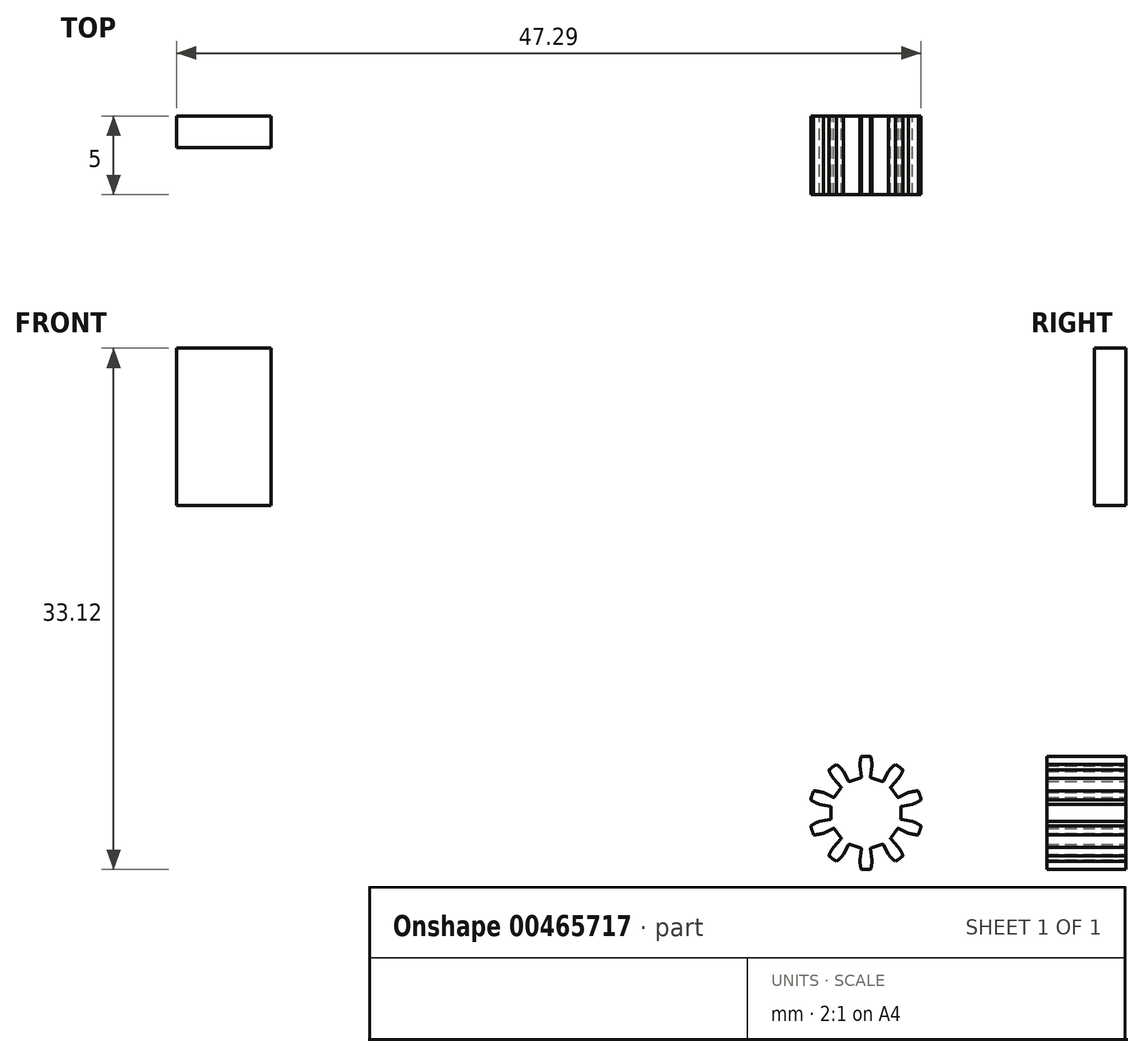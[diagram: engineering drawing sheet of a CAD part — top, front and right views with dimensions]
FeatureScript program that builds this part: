
annotation { "Feature Type Name" : "Feature", "Feature Type Description" : "" }
export const myFeature = defineFeature(function(context is Context, id is Id, definition is map)
    precondition{}
    {
        {
            var Q0;
            Q0=qCreatedBy(makeId("Front.planeOp"),FACE);
            var sketch = newSketch(context, id + "F0", { "sketchPlane" : qUnion([Q0])});
            skCircle(sketch, "E0", {"center": v(0, 0) * mm, "radius": 1.5 * mm, "construction": true});
            skCircle(sketch, "E1", {"center": v(0, 0) * mm, "radius": 3 * mm, "construction": true});
            skCircle(sketch, "E2", {"center": v(0, 0) * mm, "radius": 3.6 * mm, "construction": true});
            skCircle(sketch, "E3", {"center": v(0, 0) * mm, "radius": 2.25 * mm, "construction": true});
            skLineSegment(sketch, "E4", {"start": v(0, 0) * mm, "end": v(0, 4.8) * mm, "construction": true});
            skLineSegment(sketch, "E5", {"start": v(0, 0) * mm, "end": v(-2.88, 3.97) * mm, "construction": true});
            skLineSegment(sketch, "E6", {"start": v(0, 0) * mm, "end": v(2.78, 3.82) * mm, "construction": true});
            skArc(sketch, "E7", {"start": v(0.3, 3.59) * mm, "mid": v(0, 3.6) * mm, "end": v(-0.3, 3.59) * mm});
            skArc(sketch, "E8", {"start": v(-0.3, 3.59) * mm, "mid": v(-0.36, 3.28) * mm, "end": v(-0.4, 2.97) * mm});
            skArc(sketch, "E9", {"start": v(-1.43, 2.64) * mm, "mid": v(-1.63, 2.87) * mm, "end": v(-1.87, 3.08) * mm});
            skArc(sketch, "E10", {"start": v(-1.87, 3.08) * mm, "mid": v(-2.12, 2.91) * mm, "end": v(-2.35, 2.73) * mm});
            skLineSegment(sketch, "E11", {"start": v(0, 0) * mm, "end": v(-5.07, 1.65) * mm, "construction": true});
            skArc(sketch, "E12.MirrorCS", {"start": v(0.3, 3.59) * mm, "mid": v(0.36, 3.28) * mm, "end": v(0.4, 2.97) * mm});
            skArc(sketch, "E13.MirrorCS", {"start": v(1.43, 2.64) * mm, "mid": v(1.63, 2.87) * mm, "end": v(1.87, 3.08) * mm});
            skArc(sketch, "E14.MirrorCS", {"start": v(1.87, 3.08) * mm, "mid": v(2.12, 2.91) * mm, "end": v(2.35, 2.73) * mm});
            skArc(sketch, "E15.MirrorCS", {"start": v(-0.3, 3.59) * mm, "mid": v(0, 3.6) * mm, "end": v(0.3, 3.59) * mm});
            skArc(sketch, "E16.MirrorCS", {"start": v(2.35, 2.73) * mm, "mid": v(2.12, 2.91) * mm, "end": v(1.87, 3.08) * mm});
            skArc(sketch, "E17.MirrorCS", {"start": v(3.5, -0.82) * mm, "mid": v(3.42, -1.11) * mm, "end": v(3.32, -1.4) * mm});
            skArc(sketch, "E18.MirrorCS", {"start": v(3.5, 0.82) * mm, "mid": v(3.24, 0.67) * mm, "end": v(2.95, 0.55) * mm});
            skArc(sketch, "E19.MirrorCS", {"start": v(2.07, 2.18) * mm, "mid": v(2.23, 2.44) * mm, "end": v(2.35, 2.73) * mm});
            skArc(sketch, "E20.MirrorCS", {"start": v(3.5, 0.82) * mm, "mid": v(3.42, 1.11) * mm, "end": v(3.32, 1.4) * mm, "construction": true});
            skArc(sketch, "E21.MirrorCS", {"start": v(2.95, -0.55) * mm, "mid": v(3.24, -0.67) * mm, "end": v(3.5, -0.82) * mm});
            skArc(sketch, "E22.MirrorCS", {"start": v(3.32, 1.4) * mm, "mid": v(3.01, 1.36) * mm, "end": v(2.7, 1.3) * mm});
            skArc(sketch, "E23.MirrorCS", {"start": v(3.32, 1.4) * mm, "mid": v(3.42, 1.11) * mm, "end": v(3.5, 0.82) * mm});
            skArc(sketch, "E24.MirrorCS", {"start": v(3.5, -0.82) * mm, "mid": v(3.24, -0.67) * mm, "end": v(2.95, -0.55) * mm});
            skArc(sketch, "E25.MirrorCS", {"start": v(2.07, -2.18) * mm, "mid": v(2.23, -2.44) * mm, "end": v(2.35, -2.73) * mm});
            skArc(sketch, "E26.MirrorCS", {"start": v(3.32, -1.4) * mm, "mid": v(3.01, -1.36) * mm, "end": v(2.7, -1.3) * mm});
            skArc(sketch, "E27.MirrorCS", {"start": v(1.43, -2.64) * mm, "mid": v(1.63, -2.87) * mm, "end": v(1.87, -3.08) * mm});
            skArc(sketch, "E28.MirrorCS", {"start": v(0.3, -3.59) * mm, "mid": v(0.36, -3.28) * mm, "end": v(0.4, -2.97) * mm});
            skArc(sketch, "E29.MirrorCS", {"start": v(3.32, -1.4) * mm, "mid": v(3.42, -1.11) * mm, "end": v(3.5, -0.82) * mm, "construction": true});
            skArc(sketch, "E30.MirrorCS", {"start": v(2.35, -2.73) * mm, "mid": v(2.12, -2.91) * mm, "end": v(1.87, -3.08) * mm});
            skArc(sketch, "E31.MirrorCS", {"start": v(1.87, -3.08) * mm, "mid": v(2.12, -2.91) * mm, "end": v(2.35, -2.73) * mm});
            skArc(sketch, "E32.MirrorCS", {"start": v(-3.5, -0.82) * mm, "mid": v(-3.24, -0.67) * mm, "end": v(-2.95, -0.55) * mm});
            skArc(sketch, "E33.MirrorCS", {"start": v(-3.5, -0.82) * mm, "mid": v(-3.42, -1.11) * mm, "end": v(-3.32, -1.4) * mm});
            skArc(sketch, "E34.MirrorCS", {"start": v(-2.95, -0.55) * mm, "mid": v(-3.24, -0.67) * mm, "end": v(-3.5, -0.82) * mm});
            skArc(sketch, "E35.MirrorCS", {"start": v(-3.5, -0.82) * mm, "mid": v(-3.42, -1.11) * mm, "end": v(-3.32, -1.4) * mm, "construction": true});
            skArc(sketch, "E36.MirrorCS", {"start": v(-3.32, -1.4) * mm, "mid": v(-3.42, -1.11) * mm, "end": v(-3.5, -0.82) * mm, "construction": true});
            skArc(sketch, "E37.MirrorCS", {"start": v(-3.5, 0.82) * mm, "mid": v(-3.42, 1.11) * mm, "end": v(-3.32, 1.4) * mm, "construction": true});
            skArc(sketch, "E38.MirrorCS", {"start": v(-3.32, -1.4) * mm, "mid": v(-3.01, -1.36) * mm, "end": v(-2.7, -1.3) * mm});
            skArc(sketch, "E39.MirrorCS", {"start": v(-2.07, -2.18) * mm, "mid": v(-2.23, -2.44) * mm, "end": v(-2.35, -2.73) * mm});
            skArc(sketch, "E40.MirrorCS", {"start": v(-3.32, 1.4) * mm, "mid": v(-3.01, 1.36) * mm, "end": v(-2.7, 1.3) * mm});
            skArc(sketch, "E41.MirrorCS", {"start": v(-1.87, -3.08) * mm, "mid": v(-2.12, -2.91) * mm, "end": v(-2.35, -2.73) * mm});
            skArc(sketch, "E42.MirrorCS", {"start": v(-1.43, -2.64) * mm, "mid": v(-1.63, -2.87) * mm, "end": v(-1.87, -3.08) * mm});
            skArc(sketch, "E43.MirrorCS", {"start": v(-3.5, 0.82) * mm, "mid": v(-3.24, 0.67) * mm, "end": v(-2.95, 0.55) * mm});
            skArc(sketch, "E44.MirrorCS", {"start": v(-2.07, 2.18) * mm, "mid": v(-2.23, 2.44) * mm, "end": v(-2.35, 2.73) * mm});
            skArc(sketch, "E45.MirrorCS", {"start": v(-0.3, 3.59) * mm, "mid": v(0, 3.6) * mm, "end": v(0.3, 3.59) * mm, "construction": true});
            skArc(sketch, "E46.MirrorCS", {"start": v(-2.35, -2.73) * mm, "mid": v(-2.12, -2.91) * mm, "end": v(-1.87, -3.08) * mm});
            skArc(sketch, "E47.MirrorCS", {"start": v(-3.32, 1.4) * mm, "mid": v(-3.42, 1.11) * mm, "end": v(-3.5, 0.82) * mm});
            skArc(sketch, "E48.MirrorCS", {"start": v(0.3, 3.59) * mm, "mid": v(0, 3.6) * mm, "end": v(-0.3, 3.59) * mm, "construction": true});
            skArc(sketch, "E49.MirrorCS", {"start": v(-2.35, 2.73) * mm, "mid": v(-2.12, 2.91) * mm, "end": v(-1.87, 3.08) * mm});
            skArc(sketch, "E50.MirrorCS", {"start": v(-0.3, -3.59) * mm, "mid": v(-0.36, -3.28) * mm, "end": v(-0.4, -2.97) * mm});
            skLineSegment(sketch, "E51.MirrorCS", {"start": v(0, 0) * mm, "end": v(-2.78, 3.82) * mm, "construction": true});
            skArc(sketch, "E52.MirrorCS", {"start": v(0.3, -3.59) * mm, "mid": v(0, -3.6) * mm, "end": v(-0.3, -3.59) * mm});
            skArc(sketch, "E53.MirrorCS", {"start": v(-0.3, -3.59) * mm, "mid": v(0, -3.6) * mm, "end": v(0.3, -3.59) * mm, "construction": true});
            skArc(sketch, "E54.MirrorCS", {"start": v(0.3, -3.59) * mm, "mid": v(0, -3.6) * mm, "end": v(-0.3, -3.59) * mm, "construction": true});
            skLineSegment(sketch, "E55", {"start": v(-1.43, 2.64) * mm, "end": v(-1.1, 2.02) * mm});
            skLineSegment(sketch, "E56", {"start": v(-1.03, 2) * mm, "end": v(-0.34, 2.22) * mm});
            skLineSegment(sketch, "E57", {"start": v(-0.3, 2.28) * mm, "end": v(-0.4, 2.97) * mm});
            skPoint(sketch, "E58.visualSharp", {"position": v(-1.07, 1.98) * mm});
            skArc(sketch, "E58.filletArc", {"start": v(-1.1, 2.02) * mm, "mid": v(-1.07, 2) * mm, "end": v(-1.03, 2) * mm});
            skPoint(sketch, "E59.visualSharp", {"position": v(-0.3, 2.23) * mm});
            skArc(sketch, "E59.filletArc", {"start": v(-0.34, 2.22) * mm, "mid": v(-0.3, 2.24) * mm, "end": v(-0.3, 2.28) * mm});
            skLineSegment(sketch, "E60", {"start": v(0, 0) * mm, "end": v(-1.43, 2.64) * mm, "construction": true});
            skLineSegment(sketch, "E61", {"start": v(0, 0) * mm, "end": v(-0.4, 2.97) * mm, "construction": true});
            skArc(sketch, "E62.MirrorCS", {"start": v(1.1, 2.02) * mm, "mid": v(1.07, 2) * mm, "end": v(1.03, 2) * mm});
            skArc(sketch, "E63.MirrorCS", {"start": v(0.34, 2.22) * mm, "mid": v(0.3, 2.24) * mm, "end": v(0.3, 2.28) * mm});
            skLineSegment(sketch, "E64.MirrorCS", {"start": v(0.3, 2.28) * mm, "end": v(0.4, 2.97) * mm});
            skPoint(sketch, "E65.MirrorP", {"position": v(1.07, 1.98) * mm});
            skLineSegment(sketch, "E66.MirrorCS", {"start": v(1.03, 2) * mm, "end": v(0.34, 2.22) * mm});
            skLineSegment(sketch, "E67.MirrorCS", {"start": v(1.43, 2.64) * mm, "end": v(1.1, 2.02) * mm});
            skPoint(sketch, "E68.MirrorP", {"position": v(0.3, 2.23) * mm});
            skArc(sketch, "E69.MirrorCS", {"start": v(-0.34, -2.22) * mm, "mid": v(-0.3, -2.24) * mm, "end": v(-0.3, -2.28) * mm});
            skArc(sketch, "E70.MirrorCS", {"start": v(-1.1, -2.02) * mm, "mid": v(-1.07, -2) * mm, "end": v(-1.03, -2) * mm});
            skArc(sketch, "E71.MirrorCS", {"start": v(-0.3, -3.59) * mm, "mid": v(0, -3.6) * mm, "end": v(0.3, -3.59) * mm});
            skArc(sketch, "E72.MirrorCS", {"start": v(0.34, -2.22) * mm, "mid": v(0.3, -2.24) * mm, "end": v(0.3, -2.28) * mm});
            skArc(sketch, "E73.MirrorCS", {"start": v(1.1, -2.02) * mm, "mid": v(1.07, -2) * mm, "end": v(1.03, -2) * mm});
            skPoint(sketch, "E74.MirrorP", {"position": v(-0.3, -2.23) * mm});
            skLineSegment(sketch, "E75.MirrorCS", {"start": v(-0.3, -2.28) * mm, "end": v(-0.4, -2.97) * mm});
            skPoint(sketch, "E76.MirrorP", {"position": v(0.3, -2.23) * mm});
            skLineSegment(sketch, "E77.MirrorCS", {"start": v(1.43, -2.64) * mm, "end": v(1.1, -2.02) * mm});
            skLineSegment(sketch, "E78.MirrorCS", {"start": v(-1.03, -2) * mm, "end": v(-0.34, -2.22) * mm});
            skPoint(sketch, "E79.MirrorP", {"position": v(1.07, -1.98) * mm});
            skPoint(sketch, "E80.MirrorP", {"position": v(-1.07, -1.98) * mm});
            skLineSegment(sketch, "E81.MirrorCS", {"start": v(-1.43, -2.64) * mm, "end": v(-1.1, -2.02) * mm});
            skLineSegment(sketch, "E82.MirrorCS", {"start": v(1.03, -2) * mm, "end": v(0.34, -2.22) * mm});
            skLineSegment(sketch, "E83.MirrorCS", {"start": v(0.3, -2.28) * mm, "end": v(0.4, -2.97) * mm});
            skArc(sketch, "E84.MirrorCS", {"start": v(3.32, -1.4) * mm, "mid": v(3.42, -1.11) * mm, "end": v(3.5, -0.82) * mm});
            skArc(sketch, "E85.MirrorCS", {"start": v(3.5, 0.82) * mm, "mid": v(3.42, 1.11) * mm, "end": v(3.32, 1.4) * mm});
            skArc(sketch, "E86.MirrorCS", {"start": v(2, 1) * mm, "mid": v(2.03, 0.99) * mm, "end": v(2.07, 0.99) * mm});
            skArc(sketch, "E87.MirrorCS", {"start": v(-3.32, -1.4) * mm, "mid": v(-3.42, -1.11) * mm, "end": v(-3.5, -0.82) * mm});
            skArc(sketch, "E88.MirrorCS", {"start": v(2.21, 0.36) * mm, "mid": v(2.23, 0.4) * mm, "end": v(2.26, 0.42) * mm});
            skArc(sketch, "E89.MirrorCS", {"start": v(3.32, 1.4) * mm, "mid": v(3.42, 1.11) * mm, "end": v(3.5, 0.82) * mm, "construction": true});
            skArc(sketch, "E90.MirrorCS", {"start": v(-2.26, 0.42) * mm, "mid": v(-2.23, 0.4) * mm, "end": v(-2.21, 0.36) * mm});
            skArc(sketch, "E91.MirrorCS", {"start": v(-3.5, 0.82) * mm, "mid": v(-3.42, 1.11) * mm, "end": v(-3.32, 1.4) * mm});
            skArc(sketch, "E92.MirrorCS", {"start": v(-2.21, -0.36) * mm, "mid": v(-2.23, -0.4) * mm, "end": v(-2.26, -0.42) * mm});
            skArc(sketch, "E93.MirrorCS", {"start": v(-2.35, 2.73) * mm, "mid": v(-2.12, 2.91) * mm, "end": v(-1.87, 3.08) * mm, "construction": true});
            skArc(sketch, "E94.MirrorCS", {"start": v(1.87, -3.08) * mm, "mid": v(2.12, -2.91) * mm, "end": v(2.35, -2.73) * mm, "construction": true});
            skArc(sketch, "E95.MirrorCS", {"start": v(-1.58, -1.67) * mm, "mid": v(-1.57, -1.63) * mm, "end": v(-1.58, -1.6) * mm});
            skArc(sketch, "E96.MirrorCS", {"start": v(2.26, -0.42) * mm, "mid": v(2.23, -0.4) * mm, "end": v(2.21, -0.36) * mm});
            skArc(sketch, "E97.MirrorCS", {"start": v(-2, -1) * mm, "mid": v(-2.03, -0.99) * mm, "end": v(-2.07, -0.99) * mm});
            skArc(sketch, "E98.MirrorCS", {"start": v(1.58, 1.67) * mm, "mid": v(1.57, 1.63) * mm, "end": v(1.58, 1.6) * mm});
            skArc(sketch, "E99.MirrorCS", {"start": v(-1.87, 3.08) * mm, "mid": v(-1.63, 2.87) * mm, "end": v(-1.43, 2.64) * mm});
            skArc(sketch, "E100.MirrorCS", {"start": v(0.4, -2.97) * mm, "mid": v(0.36, -3.28) * mm, "end": v(0.3, -3.59) * mm});
            skArc(sketch, "E101.MirrorCS", {"start": v(-2.95, 0.55) * mm, "mid": v(-3.24, 0.67) * mm, "end": v(-3.5, 0.82) * mm});
            skLineSegment(sketch, "E102.MirrorCS", {"start": v(2.21, -0.36) * mm, "end": v(2.21, 0.36) * mm});
            skLineSegment(sketch, "E103.MirrorCS", {"start": v(2.26, 0.42) * mm, "end": v(2.95, 0.55) * mm});
            skArc(sketch, "E104.MirrorCS", {"start": v(-2.7, 1.3) * mm, "mid": v(-3.01, 1.36) * mm, "end": v(-3.32, 1.4) * mm});
            skArc(sketch, "E105.MirrorCS", {"start": v(-2.35, 2.73) * mm, "mid": v(-2.23, 2.44) * mm, "end": v(-2.07, 2.18) * mm});
            skLineSegment(sketch, "E106.MirrorCS", {"start": v(2.95, -0.55) * mm, "end": v(2.26, -0.42) * mm});
            skLineSegment(sketch, "E107.MirrorCS", {"start": v(0, 0) * mm, "end": v(4.66, -1.52) * mm, "construction": true});
            skArc(sketch, "E108.MirrorCS", {"start": v(2.35, -2.73) * mm, "mid": v(2.23, -2.44) * mm, "end": v(2.07, -2.18) * mm});
            skArc(sketch, "E109.MirrorCS", {"start": v(1.87, -3.08) * mm, "mid": v(1.63, -2.87) * mm, "end": v(1.43, -2.64) * mm});
            skLineSegment(sketch, "E110.MirrorCS", {"start": v(0, 0) * mm, "end": v(4.56, 1.48) * mm, "construction": true});
            skArc(sketch, "E111.MirrorCS", {"start": v(2.7, -1.3) * mm, "mid": v(3.01, -1.36) * mm, "end": v(3.32, -1.4) * mm});
            skPoint(sketch, "E112.MirrorP", {"position": v(2.21, -0.4) * mm});
            skLineSegment(sketch, "E113.MirrorCS", {"start": v(0, 0) * mm, "end": v(4.5, -1.46) * mm, "construction": true});
            skLineSegment(sketch, "E114.MirrorCS", {"start": v(-2.95, 0.55) * mm, "end": v(-2.26, 0.42) * mm});
            skLineSegment(sketch, "E115.MirrorCS", {"start": v(-2.07, -0.99) * mm, "end": v(-2.7, -1.3) * mm});
            skPoint(sketch, "E116.MirrorP", {"position": v(-2.21, -0.4) * mm});
            skPoint(sketch, "E117.MirrorP", {"position": v(-2.21, 0.4) * mm});
            skLineSegment(sketch, "E118.MirrorCS", {"start": v(-1.58, -1.6) * mm, "end": v(-2, -1) * mm});
            skLineSegment(sketch, "E119.MirrorCS", {"start": v(-2.26, -0.42) * mm, "end": v(-2.95, -0.55) * mm});
            skLineSegment(sketch, "E120.MirrorCS", {"start": v(0, 0) * mm, "end": v(2.95, 0.55) * mm, "construction": true});
            skLineSegment(sketch, "E121.MirrorCS", {"start": v(2.07, 0.99) * mm, "end": v(2.7, 1.3) * mm});
            skPoint(sketch, "E122.MirrorP", {"position": v(1.55, 1.63) * mm});
            skPoint(sketch, "E123.MirrorP", {"position": v(2.21, 0.4) * mm});
            skLineSegment(sketch, "E124.MirrorCS", {"start": v(1.58, 1.6) * mm, "end": v(2, 1) * mm});
            skLineSegment(sketch, "E125.MirrorCS", {"start": v(2.07, 2.18) * mm, "end": v(1.58, 1.67) * mm});
            skPoint(sketch, "E126.MirrorP", {"position": v(-2.03, -0.97) * mm});
            skLineSegment(sketch, "E127.MirrorCS", {"start": v(0, 0) * mm, "end": v(2.95, -0.55) * mm, "construction": true});
            skPoint(sketch, "E128.MirrorP", {"position": v(2.03, 0.97) * mm});
            skPoint(sketch, "E129.MirrorP", {"position": v(-1.55, -1.63) * mm});
            skLineSegment(sketch, "E130.MirrorCS", {"start": v(-2.07, -2.18) * mm, "end": v(-1.58, -1.67) * mm});
            skLineSegment(sketch, "E131.MirrorCS", {"start": v(-2.21, 0.36) * mm, "end": v(-2.21, -0.36) * mm});
            skArc(sketch, "E132.MirrorCS", {"start": v(3.5, -0.82) * mm, "mid": v(3.42, -1.11) * mm, "end": v(3.32, -1.4) * mm, "construction": true});
            skArc(sketch, "E133.MirrorCS", {"start": v(2.35, 2.73) * mm, "mid": v(2.12, 2.91) * mm, "end": v(1.87, 3.08) * mm, "construction": true});
            skArc(sketch, "E134.MirrorCS", {"start": v(-3.32, 1.4) * mm, "mid": v(-3.42, 1.11) * mm, "end": v(-3.5, 0.82) * mm, "construction": true});
            skArc(sketch, "E135.MirrorCS", {"start": v(-1.87, -3.08) * mm, "mid": v(-2.12, -2.91) * mm, "end": v(-2.35, -2.73) * mm, "construction": true});
            skArc(sketch, "E136.MirrorCS", {"start": v(-0.4, -2.97) * mm, "mid": v(-0.36, -3.28) * mm, "end": v(-0.3, -3.59) * mm});
            skArc(sketch, "E137.MirrorCS", {"start": v(1.87, 3.08) * mm, "mid": v(1.63, 2.87) * mm, "end": v(1.43, 2.64) * mm});
            skArc(sketch, "E138.MirrorCS", {"start": v(2, -1) * mm, "mid": v(2.03, -0.99) * mm, "end": v(2.07, -0.99) * mm});
            skArc(sketch, "E139.MirrorCS", {"start": v(-1.58, 1.67) * mm, "mid": v(-1.57, 1.63) * mm, "end": v(-1.58, 1.6) * mm});
            skArc(sketch, "E140.MirrorCS", {"start": v(2.26, 0.42) * mm, "mid": v(2.23, 0.4) * mm, "end": v(2.21, 0.36) * mm});
            skArc(sketch, "E141.MirrorCS", {"start": v(-2, 1) * mm, "mid": v(-2.03, 0.99) * mm, "end": v(-2.07, 0.99) * mm});
            skArc(sketch, "E142.MirrorCS", {"start": v(-2.21, 0.36) * mm, "mid": v(-2.23, 0.4) * mm, "end": v(-2.26, 0.42) * mm});
            skArc(sketch, "E143.MirrorCS", {"start": v(-2.26, -0.42) * mm, "mid": v(-2.23, -0.4) * mm, "end": v(-2.21, -0.36) * mm});
            skArc(sketch, "E144.MirrorCS", {"start": v(1.58, -1.67) * mm, "mid": v(1.57, -1.63) * mm, "end": v(1.58, -1.6) * mm});
            skArc(sketch, "E145.MirrorCS", {"start": v(-2.7, -1.3) * mm, "mid": v(-3.01, -1.36) * mm, "end": v(-3.32, -1.4) * mm});
            skArc(sketch, "E146.MirrorCS", {"start": v(-2.35, -2.73) * mm, "mid": v(-2.23, -2.44) * mm, "end": v(-2.07, -2.18) * mm});
            skArc(sketch, "E147.MirrorCS", {"start": v(2.21, -0.36) * mm, "mid": v(2.23, -0.4) * mm, "end": v(2.26, -0.42) * mm});
            skArc(sketch, "E148.MirrorCS", {"start": v(-1.87, -3.08) * mm, "mid": v(-1.63, -2.87) * mm, "end": v(-1.43, -2.64) * mm});
            skLineSegment(sketch, "E149.MirrorCS", {"start": v(0, 0) * mm, "end": v(2.88, 3.97) * mm, "construction": true});
            skLineSegment(sketch, "E150.MirrorCS", {"start": v(-2.95, -0.55) * mm, "end": v(-2.26, -0.42) * mm});
            skLineSegment(sketch, "E151.MirrorCS", {"start": v(0, 0) * mm, "end": v(-4.5, -1.46) * mm, "construction": true});
            skArc(sketch, "E152.MirrorCS", {"start": v(2.35, 2.73) * mm, "mid": v(2.23, 2.44) * mm, "end": v(2.07, 2.18) * mm});
            skLineSegment(sketch, "E153.MirrorCS", {"start": v(-2.26, 0.42) * mm, "end": v(-2.95, 0.55) * mm});
            skArc(sketch, "E154.MirrorCS", {"start": v(2.7, 1.3) * mm, "mid": v(3.01, 1.36) * mm, "end": v(3.32, 1.4) * mm});
            skLineSegment(sketch, "E155.MirrorCS", {"start": v(0, 0) * mm, "end": v(-4.56, 1.48) * mm, "construction": true});
            skArc(sketch, "E156.MirrorCS", {"start": v(2.95, 0.55) * mm, "mid": v(3.24, 0.67) * mm, "end": v(3.5, 0.82) * mm});
            skLineSegment(sketch, "E157.MirrorCS", {"start": v(0, 0) * mm, "end": v(-4.66, -1.52) * mm, "construction": true});
            skPoint(sketch, "E158.MirrorP", {"position": v(-2.03, 0.97) * mm});
            skLineSegment(sketch, "E159.MirrorCS", {"start": v(2.07, -0.99) * mm, "end": v(2.7, -1.3) * mm});
            skLineSegment(sketch, "E160.MirrorCS", {"start": v(-2.07, 2.18) * mm, "end": v(-1.58, 1.67) * mm});
            skLineSegment(sketch, "E161.MirrorCS", {"start": v(0, 0) * mm, "end": v(5.07, 1.65) * mm, "construction": true});
            skLineSegment(sketch, "E162.MirrorCS", {"start": v(2.95, 0.55) * mm, "end": v(2.26, 0.42) * mm});
            skLineSegment(sketch, "E163.MirrorCS", {"start": v(-1.58, 1.6) * mm, "end": v(-2, 1) * mm});
            skPoint(sketch, "E164.MirrorP", {"position": v(2.03, -0.97) * mm});
            skLineSegment(sketch, "E165.MirrorCS", {"start": v(0, 0) * mm, "end": v(0.4, 2.97) * mm, "construction": true});
            skLineSegment(sketch, "E166.MirrorCS", {"start": v(-2.07, 0.99) * mm, "end": v(-2.7, 1.3) * mm});
            skLineSegment(sketch, "E167.MirrorCS", {"start": v(0, 0) * mm, "end": v(-2.95, -0.55) * mm, "construction": true});
            skLineSegment(sketch, "E168.MirrorCS", {"start": v(2.26, -0.42) * mm, "end": v(2.95, -0.55) * mm});
            skPoint(sketch, "E169.MirrorP", {"position": v(1.55, -1.63) * mm});
            skLineSegment(sketch, "E170.MirrorCS", {"start": v(0, 0) * mm, "end": v(-2.95, 0.55) * mm, "construction": true});
            skLineSegment(sketch, "E171.MirrorCS", {"start": v(2.07, -2.18) * mm, "end": v(1.58, -1.67) * mm});
            skLineSegment(sketch, "E172.MirrorCS", {"start": v(-2.21, -0.36) * mm, "end": v(-2.21, 0.36) * mm});
            skPoint(sketch, "E173.MirrorP", {"position": v(-1.55, 1.63) * mm});
            skLineSegment(sketch, "E174.MirrorCS", {"start": v(1.58, -1.6) * mm, "end": v(2, -1) * mm});
            skLineSegment(sketch, "E175.MirrorCS", {"start": v(0, 0) * mm, "end": v(1.43, 2.64) * mm, "construction": true});
            skLineSegment(sketch, "E176.MirrorCS", {"start": v(2.21, 0.36) * mm, "end": v(2.21, -0.36) * mm});
            skSolve(sketch);
        }
        {
            var Q0;
            Q0=makeQuery(id+"F0.imprint","IMPRINT",FACE,{"disambiguationData":[TD([[makeQuery(id+"F0.imprint","IMPRINT",EDGE,{"derivedFrom":sQuery(id+"F0.wireOp",EDGE,"E86.MirrorCS")}),-1.0]])]});
            extrude(context, id + "F1", {"entities" : qUnion([Q0]), "depth" : 5 * mm});
        }
        {
            var Q0;
            Q0=qCreatedBy(makeId("Front.planeOp"),FACE);
            var sketch = newSketch(context, id + "F2", { "sketchPlane" : qUnion([Q0])});
            skLineSegment(sketch, "E177.bottom", {"start": v(-43.8, 19.52) * mm, "end": v(-37.8, 19.52) * mm});
            skLineSegment(sketch, "E177.top", {"start": v(-43.8, 29.52) * mm, "end": v(-37.8, 29.52) * mm});
            skLineSegment(sketch, "E177.left", {"start": v(-43.8, 19.52) * mm, "end": v(-43.8, 29.52) * mm});
            skLineSegment(sketch, "E177.right", {"start": v(-37.8, 19.52) * mm, "end": v(-37.8, 29.52) * mm});
            skSolve(sketch);
        }
        {
            var Q0;
            Q0=makeQuery(id+"F2.imprint","IMPRINT",FACE,{"disambiguationData":[TD([[makeQuery(id+"F2.imprint","IMPRINT",EDGE,{"derivedFrom":sQuery(id+"F2.wireOp",EDGE,"E177.bottom")}),1.0]])]});
            extrude(context, id + "F3", {"entities" : qUnion([Q0]), "depth" : 2 * mm});
        }
    });
